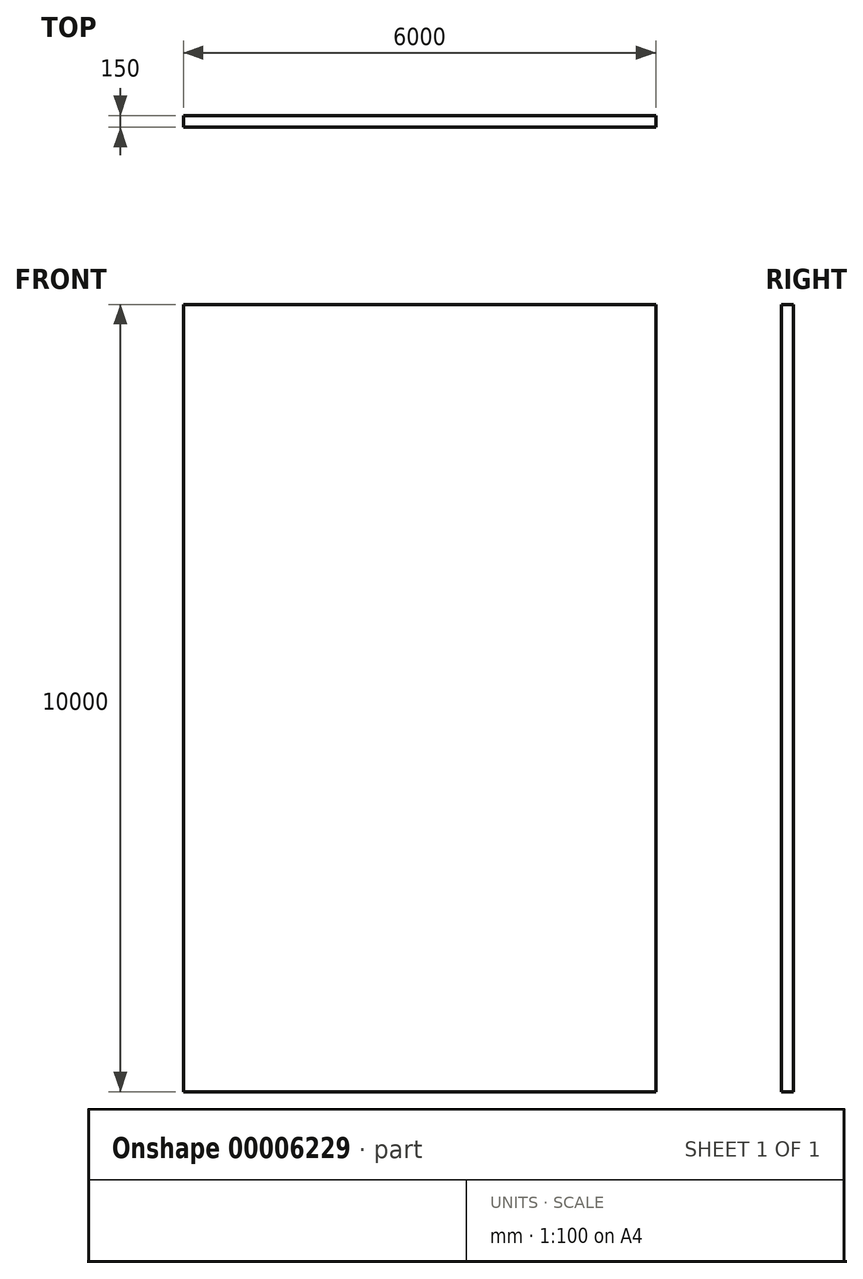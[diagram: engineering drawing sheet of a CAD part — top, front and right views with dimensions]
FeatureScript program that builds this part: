
annotation { "Feature Type Name" : "Feature", "Feature Type Description" : "" }
export const myFeature = defineFeature(function(context is Context, id is Id, definition is map)
    precondition{}
    {
        {
            var Q0;
            Q0=qCreatedBy(makeId("Front.planeOp"),FACE);
            var sketch = newSketch(context, id + "F0", { "sketchPlane" : qUnion([Q0])});
            skLineSegment(sketch, "E0.rect.bottom", {"start": v(3000, -5000) * mm, "end": v(-3000, -5000) * mm});
            skLineSegment(sketch, "E0.rect.top", {"start": v(3000, 5000) * mm, "end": v(-3000, 5000) * mm});
            skLineSegment(sketch, "E0.rect.left", {"start": v(3000, -5000) * mm, "end": v(3000, 5000) * mm});
            skLineSegment(sketch, "E0.rect.right", {"start": v(-3000, -5000) * mm, "end": v(-3000, 5000) * mm});
            skPoint(sketch, "E0.rect.middle", {"position": v(0, 0) * mm});
            skSolve(sketch);
        }
        {
            var Q0;
            Q0=makeQuery(id+"F0.imprint","IMPRINT",FACE,{"disambiguationData":[TD([[makeQuery(id+"F0.imprint","IMPRINT",EDGE,{"derivedFrom":sQuery(id+"F0.wireOp",EDGE,"E0.rect.bottom")}),-1.0]])]});
            extrude(context, id + "F1", {"entities" : qUnion([Q0]), "depth" : 150 * mm});
        }
    });
